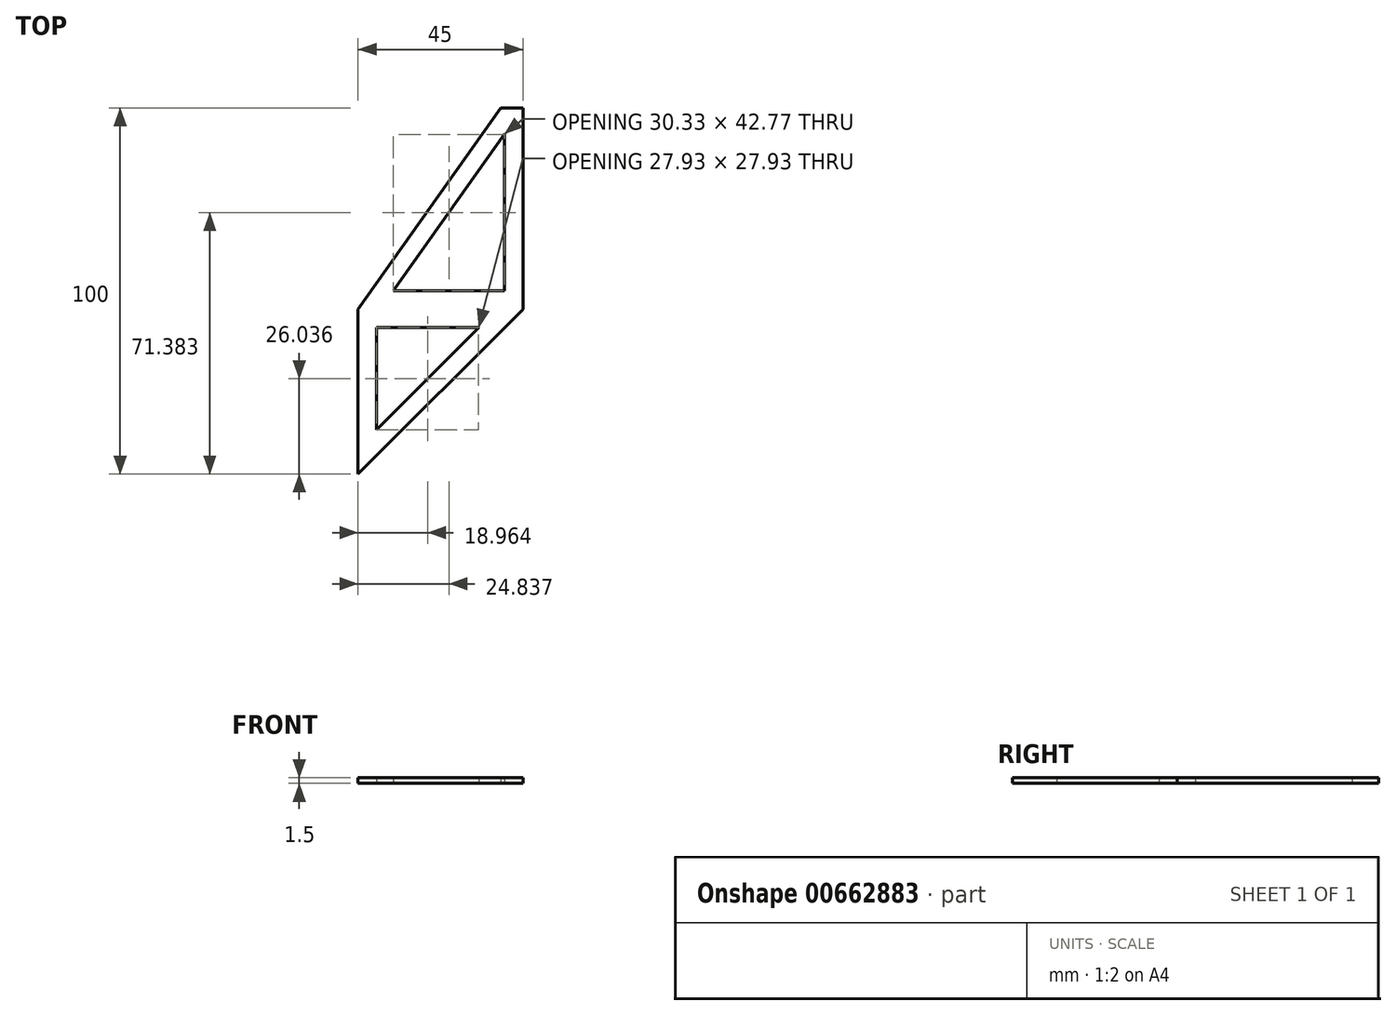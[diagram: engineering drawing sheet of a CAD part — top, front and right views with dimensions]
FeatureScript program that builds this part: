
annotation { "Feature Type Name" : "Feature", "Feature Type Description" : "" }
export const myFeature = defineFeature(function(context is Context, id is Id, definition is map)
    precondition{}
    {
        {
            var Q0;
            Q0=qCreatedBy(makeId("Top.planeOp"),FACE);
            var sketch = newSketch(context, id + "F0", { "sketchPlane" : qUnion([Q0])});
            skLineSegment(sketch, "E0", {"start": v(0, 0) * mm, "end": v(45, 0) * mm});
            skLineSegment(sketch, "E1", {"start": v(45, 0) * mm, "end": v(45, 55) * mm});
            skLineSegment(sketch, "E2", {"start": v(45, 55) * mm, "end": v(39, 55) * mm});
            skLineSegment(sketch, "E3", {"start": v(39, 55) * mm, "end": v(0, 0) * mm});
            skLineSegment(sketch, "E4", {"start": v(0, -45) * mm, "end": v(45, 0) * mm});
            skLineSegment(sketch, "E5", {"start": v(0, 0) * mm, "end": v(0, -45) * mm});
            skLineSegment(sketch, "E6.0", {"start": v(40, 47.77) * mm, "end": v(9.67, 5) * mm});
            skLineSegment(sketch, "E6.1", {"start": v(40, 5) * mm, "end": v(40, 47.77) * mm});
            skLineSegment(sketch, "E6.2", {"start": v(9.67, 5) * mm, "end": v(40, 5) * mm});
            skLineSegment(sketch, "E7.0", {"start": v(5, -5) * mm, "end": v(5, -32.93) * mm});
            skLineSegment(sketch, "E7.1", {"start": v(5, -5) * mm, "end": v(32.93, -5) * mm});
            skLineSegment(sketch, "E7.2", {"start": v(5, -32.93) * mm, "end": v(32.93, -5) * mm});
            skSolve(sketch);
        }
        {
            var Q0;
            Q0 = qSketchRegion(id + "F0", true);
            extrude(context, id + "F1", {"entities" : qUnion([Q0]), "depth" : 1.5 * mm, "offsetDistance" : 25 * mm});
        }
    });
